FCSTD DOCUMENT  (FreeCAD 0.19R24276 (Git))
Label: Base_rear-gears_017
License: All rights reserved
LicenseURL: http://en.wikipedia.org/wiki/All_rights_reserved
objects: Part::Cylinder×88, Part::Cut×43, Part::Compound×26, Part::FeaturePython×15, Part::Box×12, Sketcher::SketchObject×7, PartDesign::Revolution×7, PartDesign::Body×7, Part::Common×6, Part::Chamfer×2, Mesh::Feature×2, Part::MultiFuse×1
note: 221 computed .brp shape members not serialized (recipe doc carries the construction recipe); baked Part::Feature solids carry a one-line shape summary decoded from their .brp

FEATURE [Part::FeaturePython] bevelgear008  # WARN: FeaturePython — macro-defined, semantics opaque (R4)
  AttacherType = Attacher::AttachEngine3D
  Placement = pos=(38,0,-244) rot=(0,-1,0;1.5708rad)
  backlash = 0.1
  beta = 12
  clearance = 0.1
  height = 30
  module = 2
  numpoints = 6
  pitch_angle = 17.29
  pressure_angle = 25
  reset_origin = true
  teeth = 13
  version = 0.0.3
FEATURE [Part::FeaturePython] Tube007  # WARN: FeaturePython — macro-defined, semantics opaque (R4)
  AttacherType = Attacher::AttachEngine3D
  Height = 40
  InnerRadius = 4.15
  OuterRadius = 8.45
  Placement = pos=(200,0,-15) rot=(0,0,1;0rad)
FEATURE [Sketcher::SketchObject] Sketch012
  FullyConstrained = false
  MapMode = 5
  Placement = pos=(0,0,0) rot=(1,0,0;1.5708rad)
  Support = -> [XZ_Plane012]
  sketch-geometry (29):
    g0: LineSegment StartX=0 StartY=-49.6356 StartZ=0 EndX=22.5 EndY=-49.6356 EndZ=0
    g1: LineSegment StartX=22.5 StartY=-49.6356 StartZ=0 EndX=22.5 EndY=-53.6356 EndZ=0
    g2: LineSegment StartX=22.5 StartY=-53.6356 StartZ=0 EndX=0 EndY=-53.6356 EndZ=0
    g3: LineSegment StartX=0 StartY=-53.6356 StartZ=0 EndX=0 EndY=-49.6356 EndZ=0
    g4: LineSegment StartX=22.5 StartY=-49.6356 StartZ=0 EndX=26.5 EndY=-49.6356 EndZ=0
    g5: LineSegment StartX=26.5 StartY=-49.6356 StartZ=0 EndX=26.5 EndY=-42.6356 EndZ=0
    g6: LineSegment StartX=26.5 StartY=-42.6356 StartZ=0 EndX=22.5 EndY=-42.6356 EndZ=0
    g7: LineSegment StartX=22.5 StartY=-42.6356 StartZ=0 EndX=22.5 EndY=-49.6356 EndZ=0
    g8: LineSegment StartX=22.5 StartY=-49.6356 StartZ=0 EndX=0 EndY=-49.6356 EndZ=0
    g9: LineSegment StartX=0 StartY=-49.6356 StartZ=0 EndX=0 EndY=-42.6356 EndZ=0
    g10: LineSegment StartX=0 StartY=-42.6356 StartZ=0 EndX=22.5 EndY=-42.6356 EndZ=0
    g11: LineSegment StartX=22.5 StartY=-42.6356 StartZ=0 EndX=22.5 EndY=-49.6356 EndZ=0
    g12: LineSegment StartX=0 StartY=-42.6356 StartZ=0 EndX=22.5 EndY=-49.6356 EndZ=0
    g13: LineSegment StartX=22.5 StartY=-49.6356 StartZ=0 EndX=21.9059 EndY=-51.5453 EndZ=0
    g14: LineSegment StartX=22.5 StartY=-49.6356 StartZ=0 EndX=23.0941 EndY=-47.7259 EndZ=0
    g15: LineSegment StartX=23.0941 StartY=-47.7259 StartZ=0 EndX=0 EndY=-42.6356 EndZ=0
    g16: LineSegment StartX=21.9059 StartY=-51.5453 StartZ=0 EndX=0 EndY=-42.6356 EndZ=0
    g17: LineSegment StartX=23.0941 StartY=-47.7259 StartZ=0 EndX=15.2817 EndY=-46.0039 EndZ=0
    g18: LineSegment StartX=15.2817 StartY=-46.0039 StartZ=0 EndX=14.1518 EndY=-49.6356 EndZ=0
    g19: LineSegment StartX=15.2817 StartY=-42.6356 StartZ=0 EndX=15.2817 EndY=-46.0039 EndZ=0
    g20: LineSegment StartX=21.9059 StartY=-51.5453 StartZ=0 EndX=21.9059 EndY=-53.6356 EndZ=0
    g21: LineSegment StartX=23.0941 StartY=-47.7259 StartZ=0 EndX=26.5 EndY=-47.7259 EndZ=0
    g22: LineSegment StartX=15.2817 StartY=-42.6356 StartZ=0 EndX=15.2817 EndY=-46.5709 EndZ=0
    g23: LineSegment StartX=15.2817 StartY=-46.5709 StartZ=0 EndX=14.4998 EndY=-48.5171 EndZ=0
    g24: LineSegment StartX=14.4998 StartY=-48.5171 StartZ=0 EndX=21.9059 EndY=-51.5453 EndZ=0
    g25: LineSegment StartX=26.275 StartY=-49.2912 StartZ=0 EndX=26.5 EndY=-42.6356 EndZ=0
    g26: LineSegment StartX=26.5 StartY=-42.6356 StartZ=0 EndX=15.2817 EndY=-42.6356 EndZ=0
    g27: LineSegment StartX=26.275 StartY=-49.2912 StartZ=0 EndX=26.275 EndY=-53.3318 EndZ=0
    g28: LineSegment StartX=21.9059 StartY=-51.5453 StartZ=0 EndX=26.275 EndY=-53.3318 EndZ=0
  constraints (77):
    c: Coincident(g0,g1)
    c: Coincident(g1,g2)
    c: Coincident(g2,g3)
    c: Coincident(g3,g0)
    c: Horizontal(g0)
    c: Horizontal(g2)
    c: Vertical(g1)
    c: Vertical(g3)
    c: PointOnObject(g0,g-2)
    c: Distance(g0) = 22.5
    c: Distance(g1) = 4
    c: Coincident(g4,g5)
    c: Coincident(g5,g6)
    c: Coincident(g6,g7)
    c: Coincident(g7,g4)
    c: Horizontal(g4)
    c: Horizontal(g6)
    c: Vertical(g5)
    c: Vertical(g7)
    c: Coincident(g4,g0)
    c: Distance(g7) = 7
    c: Distance(g6) = 4
    c: Coincident(g8,g9)
    c: Coincident(g9,g10)
    c: Coincident(g10,g11)
    c: Coincident(g11,g8)
    c: Horizontal(g8)
    c: Horizontal(g10)
    c: Vertical(g9)
    c: Vertical(g11)
    c: Coincident(g8,g0)
    c: PointOnObject(g9,g-2)
    c: Distance(g9) = 7
    c: Coincident(g12,g9)
    c: Coincident(g12,g0)
    c: Coincident(g13,g0)
    c: Perpendicular(g13,g12)
    c: Distance(g13) = 2
    c: Coincident(g14,g0)
    c: Distance(g14) = 2
    c: Perpendicular(g14,g12)
    c: Coincident(g15,g14)
    c: Coincident(g15,g9)
    c: Coincident(g16,g13)
    c: Coincident(g16,g9)
    c: Coincident(g17,g14)
    c: PointOnObject(g17,g15)
    c: Distance(g17) = 8
    c: Coincident(g18,g17)
    c: PointOnObject(g18,g0)
    c: Perpendicular(g18,g12)
    c: PointOnObject(g19,g10)
    c: Coincident(g19,g17)
    c: Vertical(g19)
    c: Coincident(g20,g13)
    c: PointOnObject(g20,g2)
    c: Vertical(g20)
    c: Coincident(g21,g14)
    c: PointOnObject(g21,g5)
    c: Horizontal(g21)
    c: Coincident(g19,g22)
    c: Coincident(g23,g22)
    c: PointOnObject(g23,g18)
    c: Coincident(g24,g23)
    c: Coincident(g24,g13)
    c: Coincident(g25,g5)
    c: Coincident(g26,g25)
    c: Coincident(g26,g22)
    c: Vertical(g22)
    c: Angle(g15,g10) = 0.216946
    c: Angle(g12,g10) = 0.301619
    c: Angle(g9,g12) = 1.26918
    c: Coincident(g27,g25)
    c: Vertical(g27)
    c: Coincident(g28,g24)
    c: Coincident(g28,g27)
    c: Parallel(g24,g28)
FEATURE [PartDesign::Revolution] Revolution012
  Angle = 360
  Axis = (22.5,0,0)
  Base = (0,9.5e-15,-42.6356)
  Placement = pos=(0,0,0) rot=(1,0,0;1.5708rad)
  Profile = -> Sketch012
  ReferenceAxis = -> Sketch012 [Axis10]
  Reversed = true
FEATURE [PartDesign::Body] Body010
  Group = -> [Revolution012,Sketch012]
  Origin = -> Origin010
  Placement = pos=(-9.5,0,-201.4) rot=(0,0,1;0rad)
  Tip = -> Revolution012
FEATURE [Part::Box] Box255  label="Krychle255"
  AttacherType = Attacher::AttachEngine3D
  Height = 6
  Length = 6
  Placement = pos=(196.5,-3,18) rot=(0,0,1;1.5708rad)
  Width = 2
FEATURE [Part::Cylinder] Cylinder656  label="Válec656"
  Angle = 360
  AttacherType = Attacher::AttachEngine3D
  Height = 10
  Placement = pos=(0,118,50) rot=(1,0,0;1.5708rad)
  Radius = 4.1
FEATURE [Part::Cylinder] Cylinder657  label="Válec657"
  Angle = 360
  AttacherType = Attacher::AttachEngine3D
  Height = 4
  Placement = pos=(0,110,50) rot=(1,0,0;1.5708rad)
  Radius = 10.5
FEATURE [Part::Cut] Cut265
  Base = -> Cylinder657
  Tool = -> Cylinder656
FEATURE [Part::Box] Box256  label="Krychle256"
  AttacherType = Attacher::AttachEngine3D
  Height = 40
  Length = 40
  Placement = pos=(-20,110,30) rot=(0,0,1;0rad)
  Width = 20
FEATURE [Part::Cut] Cut266
  Base = -> Cut265
  Tool = -> Box256
FEATURE [Part::Chamfer] Chamfer
  Base = -> Cut266
  Edges = 1 edges r=2.5: [Edge3]
FEATURE [Sketcher::SketchObject] Sketch011
  FullyConstrained = false
  MapMode = 5
  Placement = pos=(0,0,0) rot=(1,0,0;1.5708rad)
  Support = -> [XZ_Plane013]
  sketch-geometry (29):
    g0: LineSegment StartX=0 StartY=-49.6356 StartZ=0 EndX=22.5 EndY=-49.6356 EndZ=0
    g1: LineSegment StartX=22.5 StartY=-49.6356 StartZ=0 EndX=22.5 EndY=-53.6356 EndZ=0
    g2: LineSegment StartX=22.5 StartY=-53.6356 StartZ=0 EndX=0 EndY=-53.6356 EndZ=0
    g3: LineSegment StartX=0 StartY=-53.6356 StartZ=0 EndX=0 EndY=-49.6356 EndZ=0
    g4: LineSegment StartX=22.5 StartY=-49.6356 StartZ=0 EndX=26.5 EndY=-49.6356 EndZ=0
    g5: LineSegment StartX=26.5 StartY=-49.6356 StartZ=0 EndX=26.5 EndY=-42.6356 EndZ=0
    g6: LineSegment StartX=26.5 StartY=-42.6356 StartZ=0 EndX=22.5 EndY=-42.6356 EndZ=0
    g7: LineSegment StartX=22.5 StartY=-42.6356 StartZ=0 EndX=22.5 EndY=-49.6356 EndZ=0
    g8: LineSegment StartX=22.5 StartY=-49.6356 StartZ=0 EndX=0 EndY=-49.6356 EndZ=0
    g9: LineSegment StartX=0 StartY=-49.6356 StartZ=0 EndX=0 EndY=-42.6356 EndZ=0
    g10: LineSegment StartX=0 StartY=-42.6356 StartZ=0 EndX=22.5 EndY=-42.6356 EndZ=0
    g11: LineSegment StartX=22.5 StartY=-42.6356 StartZ=0 EndX=22.5 EndY=-49.6356 EndZ=0
    g12: LineSegment StartX=0 StartY=-42.6356 StartZ=0 EndX=22.5 EndY=-49.6356 EndZ=0
    g13: LineSegment StartX=22.5 StartY=-49.6356 StartZ=0 EndX=21.9059 EndY=-51.5453 EndZ=0
    g14: LineSegment StartX=22.5 StartY=-49.6356 StartZ=0 EndX=23.0941 EndY=-47.7259 EndZ=0
    g15: LineSegment StartX=23.0941 StartY=-47.7259 StartZ=0 EndX=0 EndY=-42.6356 EndZ=0
    g16: LineSegment StartX=21.9059 StartY=-51.5453 StartZ=0 EndX=0 EndY=-42.6356 EndZ=0
    g17: LineSegment StartX=23.0941 StartY=-47.7259 StartZ=0 EndX=15.2817 EndY=-46.0039 EndZ=0
    g18: LineSegment StartX=15.2817 StartY=-46.0039 StartZ=0 EndX=14.1518 EndY=-49.6356 EndZ=0
    g19: LineSegment StartX=15.2817 StartY=-42.6356 StartZ=0 EndX=15.2817 EndY=-46.0039 EndZ=0
    g20: LineSegment StartX=21.9059 StartY=-51.5453 StartZ=0 EndX=21.9059 EndY=-53.6356 EndZ=0
    g21: LineSegment StartX=23.0941 StartY=-47.7259 StartZ=0 EndX=26.5 EndY=-47.7259 EndZ=0
    g22: LineSegment StartX=15.2817 StartY=-42.6356 StartZ=0 EndX=15.2817 EndY=-46.5709 EndZ=0
    g23: LineSegment StartX=15.2817 StartY=-46.5709 StartZ=0 EndX=14.4998 EndY=-48.5171 EndZ=0
    g24: LineSegment StartX=14.4998 StartY=-48.5171 StartZ=0 EndX=21.9059 EndY=-51.5453 EndZ=0
    g25: LineSegment StartX=26.275 StartY=-49.2912 StartZ=0 EndX=26.5 EndY=-42.6356 EndZ=0
    g26: LineSegment StartX=26.5 StartY=-42.6356 StartZ=0 EndX=15.2817 EndY=-42.6356 EndZ=0
    g27: LineSegment StartX=26.275 StartY=-49.2912 StartZ=0 EndX=26.275 EndY=-53.3318 EndZ=0
    g28: LineSegment StartX=21.9059 StartY=-51.5453 StartZ=0 EndX=26.275 EndY=-53.3318 EndZ=0
  constraints (77):
    c: Coincident(g0,g1)
    c: Coincident(g1,g2)
    c: Coincident(g2,g3)
    c: Coincident(g3,g0)
    c: Horizontal(g0)
    c: Horizontal(g2)
    c: Vertical(g1)
    c: Vertical(g3)
    c: PointOnObject(g0,g-2)
    c: Distance(g0) = 22.5
    c: Distance(g1) = 4
    c: Coincident(g4,g5)
    c: Coincident(g5,g6)
    c: Coincident(g6,g7)
    c: Coincident(g7,g4)
    c: Horizontal(g4)
    c: Horizontal(g6)
    c: Vertical(g5)
    c: Vertical(g7)
    c: Coincident(g4,g0)
    c: Distance(g7) = 7
    c: Distance(g6) = 4
    c: Coincident(g8,g9)
    c: Coincident(g9,g10)
    c: Coincident(g10,g11)
    c: Coincident(g11,g8)
    c: Horizontal(g8)
    c: Horizontal(g10)
    c: Vertical(g9)
    c: Vertical(g11)
    c: Coincident(g8,g0)
    c: PointOnObject(g9,g-2)
    c: Distance(g9) = 7
    c: Coincident(g12,g9)
    c: Coincident(g12,g0)
    c: Coincident(g13,g0)
    c: Perpendicular(g13,g12)
    c: Distance(g13) = 2
    c: Coincident(g14,g0)
    c: Distance(g14) = 2
    c: Perpendicular(g14,g12)
    c: Coincident(g15,g14)
    c: Coincident(g15,g9)
    c: Coincident(g16,g13)
    c: Coincident(g16,g9)
    c: Coincident(g17,g14)
    c: PointOnObject(g17,g15)
    c: Distance(g17) = 8
    c: Coincident(g18,g17)
    c: PointOnObject(g18,g0)
    c: Perpendicular(g18,g12)
    c: PointOnObject(g19,g10)
    c: Coincident(g19,g17)
    c: Vertical(g19)
    c: Coincident(g20,g13)
    c: PointOnObject(g20,g2)
    c: Vertical(g20)
    c: Coincident(g21,g14)
    c: PointOnObject(g21,g5)
    c: Horizontal(g21)
    c: Coincident(g19,g22)
    c: Coincident(g23,g22)
    c: PointOnObject(g23,g18)
    c: Coincident(g24,g23)
    c: Coincident(g24,g13)
    c: Coincident(g25,g5)
    c: Coincident(g26,g25)
    c: Coincident(g26,g22)
    c: Vertical(g22)
    c: Angle(g15,g10) = 0.216946
    c: Angle(g12,g10) = 0.301619
    c: Angle(g9,g12) = 1.26918
    c: Coincident(g27,g25)
    c: Vertical(g27)
    c: Coincident(g28,g24)
    c: Coincident(g28,g27)
    c: Parallel(g24,g28)
FEATURE [PartDesign::Revolution] Revolution011
  Angle = 360
  Axis = (22.5,0,0)
  Base = (0,9.5e-15,-42.6356)
  Placement = pos=(0,0,0) rot=(1,0,0;1.5708rad)
  Profile = -> Sketch011
  ReferenceAxis = -> Sketch011 [Axis10]
  Reversed = true
FEATURE [PartDesign::Body] Body009
  Group = -> [Revolution011,Sketch011]
  Origin = -> Origin009
  Placement = pos=(-1.4,0,-201.4) rot=(0,0,1;0rad)
  Tip = -> Revolution011
FEATURE [Part::Box] Box254  label="Krychle254"
  AttacherType = Attacher::AttachEngine3D
  Height = 6
  Length = 6
  Placement = pos=(196.5,-3,12) rot=(0,0,1;1.5708rad)
  Width = 2
FEATURE [Part::Compound] Compound030
  Links = -> [Box255,Box254]
  Placement = pos=(0,0,-27) rot=(0,0,1;0rad)
FEATURE [Part::Cylinder] Cylinder655  label="Válec655"
  Angle = 360
  AttacherType = Attacher::AttachEngine3D
  Height = 100
  Placement = pos=(100,0,15) rot=(0.57735,0.57735,0.57735;2.0944rad)
  Radius = 1.5
FEATURE [Part::Box] Box253  label="Krychle253"
  AttacherType = Attacher::AttachEngine3D
  Height = 32
  Length = 2
  Placement = pos=(194.5,-4,-4) rot=(0,0,1;0rad)
  Width = 8
FEATURE [Part::MultiFuse] Fusion003
  Shapes = -> [Tube007,Box253]
FEATURE [Part::Cut] Cut263
  Base = -> Fusion003
  Tool = -> Compound030
FEATURE [Part::Cylinder] Cylinder654  label="Válec654"
  Angle = 360
  AttacherType = Attacher::AttachEngine3D
  Height = 100
  Placement = pos=(100,0,21) rot=(0.57735,0.57735,0.57735;2.0944rad)
  Radius = 1.5
FEATURE [Part::Compound] Compound031
  Links = -> [Cylinder654,Cylinder655]
  Placement = pos=(0,0,-27) rot=(0,0,1;0rad)
FEATURE [Part::Cut] Cut264  label="super_spojka003"
  Base = -> Cut263
  Placement = pos=(-200,133,50) rot=(1,0,0;1.5708rad)
  Tool = -> Compound031
FEATURE [Part::Common] Common
  Base = -> bevelgear008
  Tool = -> Body009
FEATURE [Part::Cut] Cut262
  Base = -> Common
  Placement = pos=(0,81.1,294) rot=(0,0,1;1.5708rad)
  Tool = -> Body010
FEATURE [Part::Compound] Compound032  label="Base_rear-gear-small1"
  Links = -> [Cut262,Cut264,Chamfer]
FEATURE [Sketcher::SketchObject] Sketch013
  FullyConstrained = false
  MapMode = 5
  Placement = pos=(0,0,0) rot=(1,0,0;1.5708rad)
  Support = -> [XZ_Plane014]
  sketch-geometry (29):
    g0: LineSegment StartX=0 StartY=-63.1814 StartZ=0 EndX=22.5 EndY=-63.1814 EndZ=0
    g1: LineSegment StartX=22.5 StartY=-63.1814 StartZ=0 EndX=22.5 EndY=-67.1814 EndZ=0
    g2: LineSegment StartX=22.5 StartY=-67.1814 StartZ=0 EndX=0 EndY=-67.1814 EndZ=0
    g3: LineSegment StartX=0 StartY=-67.1814 StartZ=0 EndX=0 EndY=-63.1814 EndZ=0
    g4: LineSegment StartX=22.5 StartY=-63.1814 StartZ=0 EndX=26.5 EndY=-63.1814 EndZ=0
    g5: LineSegment StartX=26.5 StartY=-63.1814 StartZ=0 EndX=26.5 EndY=-58.1814 EndZ=0
    g6: LineSegment StartX=26.5 StartY=-58.1814 StartZ=0 EndX=22.5 EndY=-58.1814 EndZ=0
    g7: LineSegment StartX=22.5 StartY=-58.1814 StartZ=0 EndX=22.5 EndY=-63.1814 EndZ=0
    g8: LineSegment StartX=22.5 StartY=-63.1814 StartZ=0 EndX=0 EndY=-63.1814 EndZ=0
    g9: LineSegment StartX=0 StartY=-63.1814 StartZ=0 EndX=0 EndY=-56.1814 EndZ=0
    g10: LineSegment StartX=0 StartY=-56.1814 StartZ=0 EndX=22.5 EndY=-56.1814 EndZ=0
    g11: LineSegment StartX=22.5 StartY=-56.1814 StartZ=0 EndX=22.5 EndY=-63.1814 EndZ=0
    g12: LineSegment StartX=0 StartY=-56.1814 StartZ=0 EndX=22.5 EndY=-63.1814 EndZ=0
    g13: LineSegment StartX=22.5 StartY=-63.1814 StartZ=0 EndX=21.9059 EndY=-65.0911 EndZ=0
    g14: LineSegment StartX=22.5 StartY=-63.1814 StartZ=0 EndX=23.0941 EndY=-61.2717 EndZ=0
    g15: LineSegment StartX=23.0941 StartY=-61.2717 StartZ=0 EndX=0 EndY=-56.1814 EndZ=0
    g16: LineSegment StartX=21.9059 StartY=-65.0911 StartZ=0 EndX=0 EndY=-56.1814 EndZ=0
    g17: LineSegment StartX=23.0941 StartY=-61.2717 StartZ=0 EndX=15.2817 EndY=-59.5497 EndZ=0
    g18: LineSegment StartX=15.2817 StartY=-59.5497 StartZ=0 EndX=14.1518 EndY=-63.1814 EndZ=0
    g19: LineSegment StartX=15.2817 StartY=-56.1814 StartZ=0 EndX=15.2817 EndY=-59.5497 EndZ=0
    g20: LineSegment StartX=21.9059 StartY=-65.0911 StartZ=0 EndX=21.9059 EndY=-67.1814 EndZ=0
    g21: LineSegment StartX=23.0941 StartY=-61.2717 StartZ=0 EndX=26.5 EndY=-61.2717 EndZ=0
    g22: LineSegment StartX=21.9059 StartY=-67.1814 StartZ=0 EndX=21.9059 EndY=-65.0911 EndZ=0
    g23: LineSegment StartX=21.9059 StartY=-65.0911 StartZ=0 EndX=23.0941 EndY=-61.2717 EndZ=0
    g24: LineSegment StartX=23.0941 StartY=-61.2717 StartZ=0 EndX=15.2817 EndY=-59.5497 EndZ=0
    g25: LineSegment StartX=15.2817 StartY=-59.5497 StartZ=0 EndX=14.1518 EndY=-63.1814 EndZ=0
    g26: LineSegment StartX=14.1518 StartY=-63.1814 StartZ=0 EndX=0 EndY=-63.1814 EndZ=0
    g27: LineSegment StartX=0 StartY=-63.1814 StartZ=0 EndX=0 EndY=-67.1814 EndZ=0
    g28: LineSegment StartX=0 StartY=-67.1814 StartZ=0 EndX=21.9059 EndY=-67.1814 EndZ=0
  constraints (77):
    c: Coincident(g0,g1)
    c: Coincident(g1,g2)
    c: Coincident(g2,g3)
    c: Coincident(g3,g0)
    c: Horizontal(g0)
    c: Horizontal(g2)
    c: Vertical(g1)
    c: Vertical(g3)
    c: PointOnObject(g0,g-2)
    c: Distance(g0) = 22.5
    c: Distance(g1) = 4
    c: Coincident(g4,g5)
    c: Coincident(g5,g6)
    c: Coincident(g6,g7)
    c: Coincident(g7,g4)
    c: Horizontal(g4)
    c: Horizontal(g6)
    c: Vertical(g5)
    c: Vertical(g7)
    c: Coincident(g4,g0)
    c: Distance(g7) = 5
    c: Distance(g6) = 4
    c: Coincident(g8,g9)
    c: Coincident(g9,g10)
    c: Coincident(g10,g11)
    c: Coincident(g11,g8)
    c: Horizontal(g8)
    c: Horizontal(g10)
    c: Vertical(g9)
    c: Vertical(g11)
    c: Coincident(g8,g0)
    c: PointOnObject(g9,g-2)
    c: Distance(g9) = 7
    c: Coincident(g12,g9)
    c: Coincident(g12,g0)
    c: Coincident(g13,g0)
    c: Perpendicular(g13,g12)
    c: Distance(g13) = 2
    c: Coincident(g14,g0)
    c: Distance(g14) = 2
    c: Perpendicular(g14,g12)
    c: Coincident(g15,g14)
    c: Coincident(g15,g9)
    c: Coincident(g16,g13)
    c: Coincident(g16,g9)
    c: Coincident(g17,g14)
    c: PointOnObject(g17,g15)
    c: Distance(g17) = 8
    c: Coincident(g18,g17)
    c: PointOnObject(g18,g0)
    c: Perpendicular(g18,g12)
    c: PointOnObject(g19,g10)
    c: Coincident(g19,g17)
    c: Vertical(g19)
    c: Coincident(g20,g13)
    c: PointOnObject(g20,g2)
    c: Vertical(g20)
    c: Coincident(g21,g14)
    c: PointOnObject(g21,g5)
    c: Horizontal(g21)
    c: Angle(g15,g10) = 0.216946
    c: Angle(g12,g10) = 0.301619
    c: Angle(g9,g12) = 1.26918
    c: Coincident(g22,g20)
    c: Coincident(g22,g13)
    c: Coincident(g22,g23)
    c: Coincident(g23,g14)
    c: Coincident(g23,g24)
    c: Coincident(g24,g17)
    c: Coincident(g24,g25)
    c: Coincident(g25,g18)
    c: Coincident(g26,g25)
    c: Coincident(g26,g0)
    c: Coincident(g27,g26)
    c: Coincident(g27,g2)
    c: Coincident(g28,g27)
    c: Coincident(g28,g22)
FEATURE [PartDesign::Revolution] Revolution013
  Angle = 360
  Axis = (0,-9e-16,4)
  Base = (0,1.49e-14,-67.1814)
  Placement = pos=(0,0,0) rot=(1,0,0;1.5708rad)
  Profile = -> Sketch013
  ReferenceAxis = -> Sketch013 [Axis3]
  Reversed = true
FEATURE [Part::Cylinder] Cylinder584  label="Válec584"
  Angle = 360
  AttacherType = Attacher::AttachEngine3D
  Height = 30
  Placement = pos=(0,72,232) rot=(0,0,1;0rad)
  Radius = 1.5
FEATURE [Part::Cylinder] Cylinder588  label="Válec588"
  Angle = 360
  AttacherType = Attacher::AttachEngine3D
  Height = 30
  Placement = pos=(-11,83,232) rot=(0,0,1;0rad)
  Radius = 1.5
FEATURE [Part::Cylinder] Cylinder590  label="Válec590"
  Angle = 360
  AttacherType = Attacher::AttachEngine3D
  Height = 30
  Placement = pos=(11,83,232) rot=(0,0,1;0rad)
  Radius = 1.5
FEATURE [Part::Cylinder] Cylinder573  label="Válec573"
  Angle = 360
  AttacherType = Attacher::AttachEngine3D
  Height = 3
  Placement = pos=(0,72,232) rot=(0,0,1;0rad)
  Radius = 3
FEATURE [Part::Cylinder] Cylinder587  label="Válec587"
  Angle = 360
  AttacherType = Attacher::AttachEngine3D
  Height = 30
  Placement = pos=(0,72,232) rot=(0,0,1;0rad)
  Radius = 1.5
FEATURE [Part::Cylinder] Cylinder589  label="Válec589"
  Angle = 360
  AttacherType = Attacher::AttachEngine3D
  Height = 30
  Placement = pos=(0,94,232) rot=(0,0,1;0rad)
  Radius = 1.5
FEATURE [Part::Compound] Compound360
  Links = -> [Cylinder588,Cylinder590,Cylinder587,Cylinder589]
FEATURE [Part::FeaturePython] bevelgear010  # WARN: FeaturePython — macro-defined, semantics opaque (R4)
  AttacherType = Attacher::AttachEngine3D
  Placement = pos=(0,0,-254.4) rot=(1,0,0;3.14159rad)
  backlash = 0
  beta = 12
  clearance = 0.1
  height = 16
  module = 0.1
  numpoints = 6
  pitch_angle = 72.71
  pressure_angle = 21
  reset_origin = true
  teeth = 36
  version = 0.0.3
FEATURE [PartDesign::Body] Body011
  Group = -> [Revolution013,Sketch013]
  Origin = -> Origin011
  Placement = pos=(0,0,-199.6) rot=(0,0,1;0rad)
  Tip = -> Revolution013
FEATURE [Part::Common] Common001
  Base = -> Body011
  Placement = pos=(0,83,507) rot=(0,0,1;0rad)
  Tool = -> bevelgear010
FEATURE [Part::Cylinder] Cylinder576  label="Válec576"
  Angle = 360
  AttacherType = Attacher::AttachEngine3D
  Height = 3
  Placement = pos=(11,83,232) rot=(0,0,1;0rad)
  Radius = 3
FEATURE [Part::Cylinder] Cylinder569  label="Válec569"
  Angle = 360
  AttacherType = Attacher::AttachEngine3D
  Height = 10
  Placement = pos=(0,83,242) rot=(0,0,1;0rad)
  Radius = 15.1
FEATURE [Part::Cylinder] Cylinder578  label="Válec578"
  Angle = 360
  AttacherType = Attacher::AttachEngine3D
  Height = 3
  Placement = pos=(-11,83,232) rot=(0,0,1;0rad)
  Radius = 3
FEATURE [Part::Cylinder] Cylinder585  label="Válec585"
  Angle = 360
  AttacherType = Attacher::AttachEngine3D
  Height = 30
  Placement = pos=(-11,83,232) rot=(0,0,1;0rad)
  Radius = 1.5
FEATURE [Part::Cylinder] Cylinder582  label="Válec582"
  Angle = 360
  AttacherType = Attacher::AttachEngine3D
  Height = 3
  Placement = pos=(0,94,232) rot=(0,0,1;0rad)
  Radius = 3
FEATURE [Part::Compound] Compound359
  Links = -> [Cylinder578,Cylinder576,Cylinder573,Cylinder582]
  Placement = pos=(0,0,17) rot=(0,0,1;0rad)
FEATURE [Part::Cylinder] Cylinder577  label="Válec577"
  Angle = 360
  AttacherType = Attacher::AttachEngine3D
  Height = 17
  Placement = pos=(0,83,252) rot=(0,0,1;0rad)
  Radius = 8
FEATURE [Part::Cylinder] Cylinder581  label="Válec581"
  Angle = 360
  AttacherType = Attacher::AttachEngine3D
  Height = 40
  Placement = pos=(0,83,232) rot=(0,0,1;0rad)
  Radius = 2.65
FEATURE [Part::Cut] Cut220
  Base = -> Cylinder577
  Tool = -> Cylinder581
FEATURE [Part::Cylinder] Cylinder583  label="Válec583"
  Angle = 360
  AttacherType = Attacher::AttachEngine3D
  Height = 30
  Placement = pos=(0,94,232) rot=(0,0,1;0rad)
  Radius = 1.5
FEATURE [Part::Cylinder] Cylinder586  label="Válec586"
  Angle = 360
  AttacherType = Attacher::AttachEngine3D
  Height = 30
  Placement = pos=(0,83,232) rot=(0,0,1;0rad)
  Radius = 2.65
FEATURE [Part::Cylinder] Cylinder580  label="Válec580"
  Angle = 360
  AttacherType = Attacher::AttachEngine3D
  Height = 30
  Placement = pos=(11,83,232) rot=(0,0,1;0rad)
  Radius = 1.5
FEATURE [Part::Compound] Compound358
  Links = -> [Cylinder585,Cylinder580,Cylinder584,Cylinder583]
FEATURE [Part::Cut] Cut221
  Base = -> Cylinder569
  Tool = -> Compound358
FEATURE [Part::Cut] Cut223
  Base = -> Cut221
  Tool = -> Compound359
FEATURE [Part::Cut] Cut226
  Base = -> Cut223
  Tool = -> Cylinder586
FEATURE [Part::Cut] Cut227
  Base = -> Common001
  Tool = -> Compound360
FEATURE [Part::Compound] Compound  label="Base_rear-gear-large-old"
  Links = -> [Cut227,Cut226,Cut220]
  Placement = pos=(0,0,-205) rot=(0,0,1;0rad)
FEATURE [Part::Cylinder] Cylinder600  label="Válec600"
  Angle = 360
  AttacherType = Attacher::AttachEngine3D
  Height = 30
  Placement = pos=(0,72,15) rot=(0,0,1;0rad)
  Radius = 1.5
FEATURE [Part::Box] Box  label="Krychle"
  AttacherType = Attacher::AttachEngine3D
  Height = 20
  Length = 6
  Placement = pos=(8,80,38) rot=(0,0,1;0rad)
  Width = 6
FEATURE [Part::Box] Box002  label="Krychle002"
  AttacherType = Attacher::AttachEngine3D
  Height = 20
  Length = 6
  Placement = pos=(-3,69,38) rot=(0,0,1;0rad)
  Width = 6
FEATURE [Part::Cylinder] Cylinder598  label="Válec598"
  Angle = 360
  AttacherType = Attacher::AttachEngine3D
  Height = 30
  Placement = pos=(0,72,15) rot=(0,0,1;0rad)
  Radius = 1.5
FEATURE [Part::Box] Box003  label="Krychle003"
  AttacherType = Attacher::AttachEngine3D
  Height = 20
  Length = 6
  Placement = pos=(-3,91,38) rot=(0,0,1;0rad)
  Width = 6
FEATURE [Part::Cylinder] Cylinder599  label="Válec599"
  Angle = 360
  AttacherType = Attacher::AttachEngine3D
  Height = 30
  Placement = pos=(0,94,15) rot=(0,0,1;0rad)
  Radius = 1.5
FEATURE [Sketcher::SketchObject] Sketch014
  FullyConstrained = false
  MapMode = 5
  Placement = pos=(0,0,0) rot=(1,0,0;1.5708rad)
  Support = -> [XZ_Plane015]
  sketch-geometry (29):
    g0: LineSegment StartX=0 StartY=-63.1814 StartZ=0 EndX=22.5 EndY=-63.1814 EndZ=0
    g1: LineSegment StartX=22.5 StartY=-63.1814 StartZ=0 EndX=22.5 EndY=-67.1814 EndZ=0
    g2: LineSegment StartX=22.5 StartY=-67.1814 StartZ=0 EndX=0 EndY=-67.1814 EndZ=0
    g3: LineSegment StartX=0 StartY=-67.1814 StartZ=0 EndX=0 EndY=-63.1814 EndZ=0
    g4: LineSegment StartX=22.5 StartY=-63.1814 StartZ=0 EndX=26.5 EndY=-63.1814 EndZ=0
    g5: LineSegment StartX=26.5 StartY=-63.1814 StartZ=0 EndX=26.5 EndY=-58.1814 EndZ=0
    g6: LineSegment StartX=26.5 StartY=-58.1814 StartZ=0 EndX=22.5 EndY=-58.1814 EndZ=0
    g7: LineSegment StartX=22.5 StartY=-58.1814 StartZ=0 EndX=22.5 EndY=-63.1814 EndZ=0
    g8: LineSegment StartX=22.5 StartY=-63.1814 StartZ=0 EndX=0 EndY=-63.1814 EndZ=0
    g9: LineSegment StartX=0 StartY=-63.1814 StartZ=0 EndX=0 EndY=-56.1814 EndZ=0
    g10: LineSegment StartX=0 StartY=-56.1814 StartZ=0 EndX=22.5 EndY=-56.1814 EndZ=0
    g11: LineSegment StartX=22.5 StartY=-56.1814 StartZ=0 EndX=22.5 EndY=-63.1814 EndZ=0
    g12: LineSegment StartX=0 StartY=-56.1814 StartZ=0 EndX=22.5 EndY=-63.1814 EndZ=0
    g13: LineSegment StartX=22.5 StartY=-63.1814 StartZ=0 EndX=21.9059 EndY=-65.0911 EndZ=0
    g14: LineSegment StartX=22.5 StartY=-63.1814 StartZ=0 EndX=23.0941 EndY=-61.2717 EndZ=0
    g15: LineSegment StartX=23.0941 StartY=-61.2717 StartZ=0 EndX=0 EndY=-56.1814 EndZ=0
    g16: LineSegment StartX=21.9059 StartY=-65.0911 StartZ=0 EndX=0 EndY=-56.1814 EndZ=0
    g17: LineSegment StartX=23.0941 StartY=-61.2717 StartZ=0 EndX=15.2817 EndY=-59.5497 EndZ=0
    g18: LineSegment StartX=15.2817 StartY=-59.5497 StartZ=0 EndX=14.1518 EndY=-63.1814 EndZ=0
    g19: LineSegment StartX=15.2817 StartY=-56.1814 StartZ=0 EndX=15.2817 EndY=-59.5497 EndZ=0
    g20: LineSegment StartX=21.9059 StartY=-65.0911 StartZ=0 EndX=21.9059 EndY=-67.1814 EndZ=0
    g21: LineSegment StartX=23.0941 StartY=-61.2717 StartZ=0 EndX=26.5 EndY=-61.2717 EndZ=0
    g22: LineSegment StartX=21.9059 StartY=-67.1814 StartZ=0 EndX=21.9059 EndY=-65.0911 EndZ=0
    g23: LineSegment StartX=21.9059 StartY=-65.0911 StartZ=0 EndX=23.0941 EndY=-61.2717 EndZ=0
    g24: LineSegment StartX=23.0941 StartY=-61.2717 StartZ=0 EndX=15.2817 EndY=-59.5497 EndZ=0
    g25: LineSegment StartX=15.2817 StartY=-59.5497 StartZ=0 EndX=14.1518 EndY=-63.1814 EndZ=0
    g26: LineSegment StartX=14.1518 StartY=-63.1814 StartZ=0 EndX=0 EndY=-63.1814 EndZ=0
    g27: LineSegment StartX=0 StartY=-63.1814 StartZ=0 EndX=0 EndY=-67.1814 EndZ=0
    g28: LineSegment StartX=0 StartY=-67.1814 StartZ=0 EndX=21.9059 EndY=-67.1814 EndZ=0
  constraints (77):
    c: Coincident(g0,g1)
    c: Coincident(g1,g2)
    c: Coincident(g2,g3)
    c: Coincident(g3,g0)
    c: Horizontal(g0)
    c: Horizontal(g2)
    c: Vertical(g1)
    c: Vertical(g3)
    c: PointOnObject(g0,g-2)
    c: Distance(g0) = 22.5
    c: Distance(g1) = 4
    c: Coincident(g4,g5)
    c: Coincident(g5,g6)
    c: Coincident(g6,g7)
    c: Coincident(g7,g4)
    c: Horizontal(g4)
    c: Horizontal(g6)
    c: Vertical(g5)
    c: Vertical(g7)
    c: Coincident(g4,g0)
    c: Distance(g7) = 5
    c: Distance(g6) = 4
    c: Coincident(g8,g9)
    c: Coincident(g9,g10)
    c: Coincident(g10,g11)
    c: Coincident(g11,g8)
    c: Horizontal(g8)
    c: Horizontal(g10)
    c: Vertical(g9)
    c: Vertical(g11)
    c: Coincident(g8,g0)
    c: PointOnObject(g9,g-2)
    c: Distance(g9) = 7
    c: Coincident(g12,g9)
    c: Coincident(g12,g0)
    c: Coincident(g13,g0)
    c: Perpendicular(g13,g12)
    c: Distance(g13) = 2
    c: Coincident(g14,g0)
    c: Distance(g14) = 2
    c: Perpendicular(g14,g12)
    c: Coincident(g15,g14)
    c: Coincident(g15,g9)
    c: Coincident(g16,g13)
    c: Coincident(g16,g9)
    c: Coincident(g17,g14)
    c: PointOnObject(g17,g15)
    c: Distance(g17) = 8
    c: Coincident(g18,g17)
    c: PointOnObject(g18,g0)
    c: Perpendicular(g18,g12)
    c: PointOnObject(g19,g10)
    c: Coincident(g19,g17)
    c: Vertical(g19)
    c: Coincident(g20,g13)
    c: PointOnObject(g20,g2)
    c: Vertical(g20)
    c: Coincident(g21,g14)
    c: PointOnObject(g21,g5)
    c: Horizontal(g21)
    c: Angle(g15,g10) = 0.216946
    c: Angle(g12,g10) = 0.301619
    c: Angle(g9,g12) = 1.26918
    c: Coincident(g22,g20)
    c: Coincident(g22,g13)
    c: Coincident(g22,g23)
    c: Coincident(g23,g14)
    c: Coincident(g23,g24)
    c: Coincident(g24,g17)
    c: Coincident(g24,g25)
    c: Coincident(g25,g18)
    c: Coincident(g26,g25)
    c: Coincident(g26,g0)
    c: Coincident(g27,g26)
    c: Coincident(g27,g2)
    c: Coincident(g28,g27)
    c: Coincident(g28,g22)
FEATURE [PartDesign::Revolution] Revolution014
  Angle = 360
  Axis = (0,-9e-16,4)
  Base = (0,1.49e-14,-67.1814)
  Placement = pos=(0,0,0) rot=(1,0,0;1.5708rad)
  Profile = -> Sketch014
  ReferenceAxis = -> Sketch014 [Axis3]
  Reversed = true
FEATURE [Part::Cylinder] Cylinder591  label="Válec591"
  Angle = 360
  AttacherType = Attacher::AttachEngine3D
  Height = 30
  Placement = pos=(-11,83,15) rot=(0,0,1;0rad)
  Radius = 1.5
FEATURE [Part::Cylinder] Cylinder595  label="Válec595"
  Angle = 360
  AttacherType = Attacher::AttachEngine3D
  Height = 30
  Placement = pos=(0,94,15) rot=(0,0,1;0rad)
  Radius = 1.5
FEATURE [Part::Cylinder] Cylinder593  label="Válec593"
  Angle = 360
  AttacherType = Attacher::AttachEngine3D
  Height = 30
  Placement = pos=(11,83,15) rot=(0,0,1;0rad)
  Radius = 1.5
FEATURE [Part::Cylinder] Cylinder592  label="Válec592"
  Angle = 360
  AttacherType = Attacher::AttachEngine3D
  Height = 30
  Placement = pos=(-11,83,15) rot=(0,0,1;0rad)
  Radius = 1.5
FEATURE [Part::Cylinder] Cylinder594  label="Válec594"
  Angle = 360
  AttacherType = Attacher::AttachEngine3D
  Height = 40
  Placement = pos=(0,83,15) rot=(0,0,1;0rad)
  Radius = 2.65
FEATURE [Part::Cylinder] Cylinder597  label="Válec597"
  Angle = 360
  AttacherType = Attacher::AttachEngine3D
  Height = 40
  Placement = pos=(0,83,15) rot=(0,0,1;0rad)
  Radius = 2.65
FEATURE [Part::Box] Box001  label="Krychle001"
  AttacherType = Attacher::AttachEngine3D
  Height = 20
  Length = 6
  Placement = pos=(-14,80,38) rot=(0,0,1;0rad)
  Width = 6
FEATURE [Part::Cylinder] Cylinder596  label="Válec596"
  Angle = 360
  AttacherType = Attacher::AttachEngine3D
  Height = 30
  Placement = pos=(11,83,15) rot=(0,0,1;0rad)
  Radius = 1.5
FEATURE [Part::FeaturePython] wormgear027  # WARN: FeaturePython — macro-defined, semantics opaque (R4)
  AttacherType = Attacher::AttachEngine3D
  Placement = pos=(0,83,32) rot=(0,0,1;0.069813rad)
  beta = 33.1113
  clearance = 0.25
  diameter = 46
  head = 0
  height = 5
  module = 1
  pressure_angle = 20
  reverse_pitch = false
  teeth = 30
  version = 0.0.3
FEATURE [Part::FeaturePython] wormgear026  # WARN: FeaturePython — macro-defined, semantics opaque (R4)
  AttacherType = Attacher::AttachEngine3D
  Placement = pos=(0,83,37) rot=(0,0,1;0.191986rad)
  beta = 33.1113
  clearance = 0.25
  diameter = 46
  head = 0
  height = 5
  module = 1
  pressure_angle = 20
  reverse_pitch = true
  teeth = 30
  version = 0.0.3
FEATURE [Part::Cylinder] Cylinder658  label="Válec658"
  Angle = 360
  AttacherType = Attacher::AttachEngine3D
  Height = 30
  Placement = pos=(0,72,232) rot=(0,0,1;0rad)
  Radius = 1.5
FEATURE [Part::Cylinder] Cylinder659  label="Válec659"
  Angle = 360
  AttacherType = Attacher::AttachEngine3D
  Height = 30
  Placement = pos=(-11,83,232) rot=(0,0,1;0rad)
  Radius = 1.5
FEATURE [Part::Cylinder] Cylinder660  label="Válec660"
  Angle = 360
  AttacherType = Attacher::AttachEngine3D
  Height = 30
  Placement = pos=(11,83,232) rot=(0,0,1;0rad)
  Radius = 1.5
FEATURE [Part::Cylinder] Cylinder661  label="Válec661"
  Angle = 360
  AttacherType = Attacher::AttachEngine3D
  Height = 3
  Placement = pos=(0,72,232) rot=(0,0,1;0rad)
  Radius = 3
FEATURE [Part::Cylinder] Cylinder662  label="Válec662"
  Angle = 360
  AttacherType = Attacher::AttachEngine3D
  Height = 30
  Placement = pos=(0,72,232) rot=(0,0,1;0rad)
  Radius = 1.5
FEATURE [Part::Cylinder] Cylinder663  label="Válec663"
  Angle = 360
  AttacherType = Attacher::AttachEngine3D
  Height = 30
  Placement = pos=(0,94,232) rot=(0,0,1;0rad)
  Radius = 1.5
FEATURE [Part::Compound] Compound363
  Links = -> [Cylinder659,Cylinder660,Cylinder662,Cylinder663]
FEATURE [Part::FeaturePython] bevelgear011  # WARN: FeaturePython — macro-defined, semantics opaque (R4)
  AttacherType = Attacher::AttachEngine3D
  Placement = pos=(0,0,-254.4) rot=(1,0,0;3.14159rad)
  backlash = 0
  beta = 12
  clearance = 0.1
  height = 16
  module = 0.1
  numpoints = 6
  pitch_angle = 72.71
  pressure_angle = 21
  reset_origin = true
  teeth = 36
  version = 0.0.3
FEATURE [Part::Compound] Compound364
  Links = -> [Box,Box001,Box002,Box003]
FEATURE [Part::Compound] Compound365
  Links = -> [Cylinder592,Cylinder593,Cylinder598,Cylinder599]
FEATURE [Part::Cut] Cut230
  Base = -> wormgear027
  Tool = -> Compound365
FEATURE [Part::Cut] Cut231
  Base = -> Cut230
  Tool = -> Cylinder594
FEATURE [Part::Cylinder] Cylinder  label="Válec"
  Angle = 360
  AttacherType = Attacher::AttachEngine3D
  Height = 10
  Placement = pos=(0,83,232) rot=(0,0,1;0rad)
  Radius = 25
FEATURE [PartDesign::Body] Body012
  Group = -> [Revolution014,Sketch014]
  Origin = -> Origin012
  Placement = pos=(0,0,-199.6) rot=(0,0,1;0rad)
  Tip = -> Revolution014
FEATURE [Part::Common] Common002
  Base = -> Body012
  Placement = pos=(0,83,507) rot=(0,0,1;0rad)
  Tool = -> bevelgear011
FEATURE [Part::Cylinder] Cylinder664  label="Válec664"
  Angle = 360
  AttacherType = Attacher::AttachEngine3D
  Height = 3
  Placement = pos=(11,83,232) rot=(0,0,1;0rad)
  Radius = 3
FEATURE [Part::Cylinder] Cylinder665  label="Válec665"
  Angle = 360
  AttacherType = Attacher::AttachEngine3D
  Height = 10
  Placement = pos=(0,83,242) rot=(0,0,1;0rad)
  Radius = 15.1
FEATURE [Part::Cylinder] Cylinder666  label="Válec666"
  Angle = 360
  AttacherType = Attacher::AttachEngine3D
  Height = 3
  Placement = pos=(-11,83,232) rot=(0,0,1;0rad)
  Radius = 3
FEATURE [Part::Cylinder] Cylinder667  label="Válec667"
  Angle = 360
  AttacherType = Attacher::AttachEngine3D
  Height = 30
  Placement = pos=(-11,83,232) rot=(0,0,1;0rad)
  Radius = 1.5
FEATURE [Part::Cylinder] Cylinder668  label="Válec668"
  Angle = 360
  AttacherType = Attacher::AttachEngine3D
  Height = 3
  Placement = pos=(0,94,232) rot=(0,0,1;0rad)
  Radius = 3
FEATURE [Part::Compound] Compound362
  Links = -> [Cylinder666,Cylinder664,Cylinder661,Cylinder668]
  Placement = pos=(0,0,17) rot=(0,0,1;0rad)
FEATURE [Part::Cylinder] Cylinder669  label="Válec669"
  Angle = 360
  AttacherType = Attacher::AttachEngine3D
  Height = 17
  Placement = pos=(0,83,252) rot=(0,0,1;0rad)
  Radius = 8
FEATURE [Part::Cylinder] Cylinder670  label="Válec670"
  Angle = 360
  AttacherType = Attacher::AttachEngine3D
  Height = 40
  Placement = pos=(0,83,232) rot=(0,0,1;0rad)
  Radius = 2.65
FEATURE [Part::Cut] Cut268
  Base = -> Cylinder669
  Tool = -> Cylinder670
FEATURE [Part::Cylinder] Cylinder671  label="Válec671"
  Angle = 360
  AttacherType = Attacher::AttachEngine3D
  Height = 30
  Placement = pos=(0,94,232) rot=(0,0,1;0rad)
  Radius = 1.5
FEATURE [Part::Cylinder] Cylinder672  label="Válec672"
  Angle = 360
  AttacherType = Attacher::AttachEngine3D
  Height = 30
  Placement = pos=(0,83,232) rot=(0,0,1;0rad)
  Radius = 2.65
FEATURE [Part::Cylinder] Cylinder673  label="Válec673"
  Angle = 360
  AttacherType = Attacher::AttachEngine3D
  Height = 30
  Placement = pos=(11,83,232) rot=(0,0,1;0rad)
  Radius = 1.5
FEATURE [Part::Compound] Compound361
  Links = -> [Cylinder667,Cylinder673,Cylinder658,Cylinder671]
FEATURE [Part::Cut] Cut269
  Base = -> Cylinder665
  Tool = -> Compound361
FEATURE [Part::Cut] Cut270
  Base = -> Cut269
  Tool = -> Compound362
FEATURE [Part::Cut] Cut267
  Base = -> Cut270
  Tool = -> Cylinder672
FEATURE [Part::Cut] Cut271
  Base = -> Common002
  Tool = -> Compound363
FEATURE [Part::Cut] Cut228
  Base = -> Cut271
  Tool = -> Cylinder
FEATURE [Part::Compound] Compound367
  Links = -> [Cylinder591,Cylinder596,Cylinder600,Cylinder595]
FEATURE [Part::Cut] Cut229
  Base = -> wormgear026
  Tool = -> Compound367
FEATURE [Part::Cut] Cut232
  Base = -> Cut229
  Tool = -> Cylinder597
FEATURE [Part::Cut] Cut233
  Base = -> Cut232
  Tool = -> Compound364
FEATURE [Part::Compound] Compound368  label="bazovina-prevod-B"
  Links = -> [Cut231,Cut233]
  Placement = pos=(0,0,200) rot=(0,0,1;0rad)
FEATURE [Part::Compound] Compound369
  Links = -> [Cut228,Cut267,Cut268]
FEATURE [Part::Compound] Compound366  label="Base_rear-gear-large"
  Links = -> [Compound369,Compound368]
  Placement = pos=(0,0,-205) rot=(0,0,1;0rad)
FEATURE [Sketcher::SketchObject] Sketch015
  FullyConstrained = false
  MapMode = 5
  Placement = pos=(0,0,0) rot=(1,0,0;1.5708rad)
  Support = -> [XZ_Plane016]
  sketch-geometry (29):
    g0: LineSegment StartX=0 StartY=-63.1814 StartZ=0 EndX=22.5 EndY=-63.1814 EndZ=0
    g1: LineSegment StartX=22.5 StartY=-63.1814 StartZ=0 EndX=22.5 EndY=-67.1814 EndZ=0
    g2: LineSegment StartX=22.5 StartY=-67.1814 StartZ=0 EndX=0 EndY=-67.1814 EndZ=0
    g3: LineSegment StartX=0 StartY=-67.1814 StartZ=0 EndX=0 EndY=-63.1814 EndZ=0
    g4: LineSegment StartX=22.5 StartY=-63.1814 StartZ=0 EndX=26.5 EndY=-63.1814 EndZ=0
    g5: LineSegment StartX=26.5 StartY=-63.1814 StartZ=0 EndX=26.5 EndY=-58.1814 EndZ=0
    g6: LineSegment StartX=26.5 StartY=-58.1814 StartZ=0 EndX=22.5 EndY=-58.1814 EndZ=0
    g7: LineSegment StartX=22.5 StartY=-58.1814 StartZ=0 EndX=22.5 EndY=-63.1814 EndZ=0
    g8: LineSegment StartX=22.5 StartY=-63.1814 StartZ=0 EndX=0 EndY=-63.1814 EndZ=0
    g9: LineSegment StartX=0 StartY=-63.1814 StartZ=0 EndX=0 EndY=-56.1814 EndZ=0
    g10: LineSegment StartX=0 StartY=-56.1814 StartZ=0 EndX=22.5 EndY=-56.1814 EndZ=0
    g11: LineSegment StartX=22.5 StartY=-56.1814 StartZ=0 EndX=22.5 EndY=-63.1814 EndZ=0
    g12: LineSegment StartX=0 StartY=-56.1814 StartZ=0 EndX=22.5 EndY=-63.1814 EndZ=0
    g13: LineSegment StartX=22.5 StartY=-63.1814 StartZ=0 EndX=21.9059 EndY=-65.0911 EndZ=0
    g14: LineSegment StartX=22.5 StartY=-63.1814 StartZ=0 EndX=23.0941 EndY=-61.2717 EndZ=0
    g15: LineSegment StartX=23.0941 StartY=-61.2717 StartZ=0 EndX=0 EndY=-56.1814 EndZ=0
    g16: LineSegment StartX=21.9059 StartY=-65.0911 StartZ=0 EndX=0 EndY=-56.1814 EndZ=0
    g17: LineSegment StartX=23.0941 StartY=-61.2717 StartZ=0 EndX=15.2817 EndY=-59.5497 EndZ=0
    g18: LineSegment StartX=15.2817 StartY=-59.5497 StartZ=0 EndX=14.1518 EndY=-63.1814 EndZ=0
    g19: LineSegment StartX=15.2817 StartY=-56.1814 StartZ=0 EndX=15.2817 EndY=-59.5497 EndZ=0
    g20: LineSegment StartX=21.9059 StartY=-65.0911 StartZ=0 EndX=21.9059 EndY=-67.1814 EndZ=0
    g21: LineSegment StartX=23.0941 StartY=-61.2717 StartZ=0 EndX=26.5 EndY=-61.2717 EndZ=0
    g22: LineSegment StartX=21.9059 StartY=-67.1814 StartZ=0 EndX=21.9059 EndY=-65.0911 EndZ=0
    g23: LineSegment StartX=21.9059 StartY=-65.0911 StartZ=0 EndX=23.0941 EndY=-61.2717 EndZ=0
    g24: LineSegment StartX=23.0941 StartY=-61.2717 StartZ=0 EndX=15.2817 EndY=-59.5497 EndZ=0
    g25: LineSegment StartX=15.2817 StartY=-59.5497 StartZ=0 EndX=14.1518 EndY=-63.1814 EndZ=0
    g26: LineSegment StartX=14.1518 StartY=-63.1814 StartZ=0 EndX=0 EndY=-63.1814 EndZ=0
    g27: LineSegment StartX=0 StartY=-63.1814 StartZ=0 EndX=0 EndY=-67.1814 EndZ=0
    g28: LineSegment StartX=0 StartY=-67.1814 StartZ=0 EndX=21.9059 EndY=-67.1814 EndZ=0
  constraints (77):
    c: Coincident(g0,g1)
    c: Coincident(g1,g2)
    c: Coincident(g2,g3)
    c: Coincident(g3,g0)
    c: Horizontal(g0)
    c: Horizontal(g2)
    c: Vertical(g1)
    c: Vertical(g3)
    c: PointOnObject(g0,g-2)
    c: Distance(g0) = 22.5
    c: Distance(g1) = 4
    c: Coincident(g4,g5)
    c: Coincident(g5,g6)
    c: Coincident(g6,g7)
    c: Coincident(g7,g4)
    c: Horizontal(g4)
    c: Horizontal(g6)
    c: Vertical(g5)
    c: Vertical(g7)
    c: Coincident(g4,g0)
    c: Distance(g7) = 5
    c: Distance(g6) = 4
    c: Coincident(g8,g9)
    c: Coincident(g9,g10)
    c: Coincident(g10,g11)
    c: Coincident(g11,g8)
    c: Horizontal(g8)
    c: Horizontal(g10)
    c: Vertical(g9)
    c: Vertical(g11)
    c: Coincident(g8,g0)
    c: PointOnObject(g9,g-2)
    c: Distance(g9) = 7
    c: Coincident(g12,g9)
    c: Coincident(g12,g0)
    c: Coincident(g13,g0)
    c: Perpendicular(g13,g12)
    c: Distance(g13) = 2
    c: Coincident(g14,g0)
    c: Distance(g14) = 2
    c: Perpendicular(g14,g12)
    c: Coincident(g15,g14)
    c: Coincident(g15,g9)
    c: Coincident(g16,g13)
    c: Coincident(g16,g9)
    c: Coincident(g17,g14)
    c: PointOnObject(g17,g15)
    c: Distance(g17) = 8
    c: Coincident(g18,g17)
    c: PointOnObject(g18,g0)
    c: Perpendicular(g18,g12)
    c: PointOnObject(g19,g10)
    c: Coincident(g19,g17)
    c: Vertical(g19)
    c: Coincident(g20,g13)
    c: PointOnObject(g20,g2)
    c: Vertical(g20)
    c: Coincident(g21,g14)
    c: PointOnObject(g21,g5)
    c: Horizontal(g21)
    c: Angle(g15,g10) = 0.216946
    c: Angle(g12,g10) = 0.301619
    c: Angle(g9,g12) = 1.26918
    c: Coincident(g22,g20)
    c: Coincident(g22,g13)
    c: Coincident(g22,g23)
    c: Coincident(g23,g14)
    c: Coincident(g23,g24)
    c: Coincident(g24,g17)
    c: Coincident(g24,g25)
    c: Coincident(g25,g18)
    c: Coincident(g26,g25)
    c: Coincident(g26,g0)
    c: Coincident(g27,g26)
    c: Coincident(g27,g2)
    c: Coincident(g28,g27)
    c: Coincident(g28,g22)
FEATURE [Part::Cylinder] Cylinder674  label="Válec674"
  Angle = 360
  AttacherType = Attacher::AttachEngine3D
  Height = 30
  Placement = pos=(0,72,15) rot=(0,0,1;0rad)
  Radius = 1.5
FEATURE [Part::Box] Box257  label="Krychle257"
  AttacherType = Attacher::AttachEngine3D
  Height = 20
  Length = 6
  Placement = pos=(-3,91,38) rot=(0,0,1;0rad)
  Width = 6
FEATURE [Part::Cylinder] Cylinder675  label="Válec675"
  Angle = 360
  AttacherType = Attacher::AttachEngine3D
  Height = 30
  Placement = pos=(0,72,15) rot=(0,0,1;0rad)
  Radius = 1.5
FEATURE [Part::Cylinder] Cylinder676  label="Válec676"
  Angle = 360
  AttacherType = Attacher::AttachEngine3D
  Height = 30
  Placement = pos=(0,94,15) rot=(0,0,1;0rad)
  Radius = 1.5
FEATURE [Part::Cylinder] Cylinder677  label="Válec677"
  Angle = 360
  AttacherType = Attacher::AttachEngine3D
  Height = 30
  Placement = pos=(11,83,15) rot=(0,0,1;0rad)
  Radius = 1.5
FEATURE [Part::Cylinder] Cylinder678  label="Válec678"
  Angle = 360
  AttacherType = Attacher::AttachEngine3D
  Height = 30
  Placement = pos=(0,94,15) rot=(0,0,1;0rad)
  Radius = 1.5
FEATURE [Part::Box] Box258  label="Krychle258"
  AttacherType = Attacher::AttachEngine3D
  Height = 20
  Length = 6
  Placement = pos=(8,80,38) rot=(0,0,1;0rad)
  Width = 6
FEATURE [Part::Cylinder] Cylinder679  label="Válec679"
  Angle = 360
  AttacherType = Attacher::AttachEngine3D
  Height = 30
  Placement = pos=(-11,83,15) rot=(0,0,1;0rad)
  Radius = 1.5
FEATURE [Part::Box] Box259  label="Krychle259"
  AttacherType = Attacher::AttachEngine3D
  Height = 20
  Length = 6
  Placement = pos=(-3,69,38) rot=(0,0,1;0rad)
  Width = 6
FEATURE [PartDesign::Revolution] Revolution015
  Angle = 360
  Axis = (0,-9e-16,4)
  Base = (0,1.49e-14,-67.1814)
  Placement = pos=(0,0,0) rot=(1,0,0;1.5708rad)
  Profile = -> Sketch015
  ReferenceAxis = -> Sketch015 [Axis3]
  Reversed = true
FEATURE [PartDesign::Body] Body013
  Group = -> [Revolution015,Sketch015]
  Origin = -> Origin013
  Placement = pos=(0,0,-199.6) rot=(0,0,1;0rad)
  Tip = -> Revolution015
FEATURE [Part::Cylinder] Cylinder680  label="Válec680"
  Angle = 360
  AttacherType = Attacher::AttachEngine3D
  Height = 40
  Placement = pos=(0,83,15) rot=(0,0,1;0rad)
  Radius = 2.65
FEATURE [Part::Cylinder] Cylinder681  label="Válec681"
  Angle = 360
  AttacherType = Attacher::AttachEngine3D
  Height = 30
  Placement = pos=(-11,83,15) rot=(0,0,1;0rad)
  Radius = 1.5
FEATURE [Part::Cylinder] Cylinder682  label="Válec682"
  Angle = 360
  AttacherType = Attacher::AttachEngine3D
  Height = 40
  Placement = pos=(0,83,15) rot=(0,0,1;0rad)
  Radius = 2.65
FEATURE [Part::Cylinder] Cylinder683  label="Válec683"
  Angle = 360
  AttacherType = Attacher::AttachEngine3D
  Height = 30
  Placement = pos=(11,83,15) rot=(0,0,1;0rad)
  Radius = 1.5
FEATURE [Part::Box] Box260  label="Krychle260"
  AttacherType = Attacher::AttachEngine3D
  Height = 20
  Length = 6
  Placement = pos=(-14,80,38) rot=(0,0,1;0rad)
  Width = 6
FEATURE [Part::Cylinder] Cylinder684  label="Válec684"
  Angle = 360
  AttacherType = Attacher::AttachEngine3D
  Height = 30
  Placement = pos=(0,72,232) rot=(0,0,1;0rad)
  Radius = 1.5
FEATURE [Part::Cylinder] Cylinder685  label="Válec685"
  Angle = 360
  AttacherType = Attacher::AttachEngine3D
  Height = 30
  Placement = pos=(-11,83,232) rot=(0,0,1;0rad)
  Radius = 1.5
FEATURE [Part::Cylinder] Cylinder686  label="Válec686"
  Angle = 360
  AttacherType = Attacher::AttachEngine3D
  Height = 30
  Placement = pos=(11,83,232) rot=(0,0,1;0rad)
  Radius = 1.5
FEATURE [Part::FeaturePython] wormgear028  # WARN: FeaturePython — macro-defined, semantics opaque (R4)
  AttacherType = Attacher::AttachEngine3D
  Placement = pos=(0,83,32) rot=(0,0,1;0.069813rad)
  beta = 33.1113
  clearance = 0.25
  diameter = 46
  head = 0
  height = 5
  module = 1
  pressure_angle = 20
  reverse_pitch = false
  teeth = 30
  version = 0.0.3
FEATURE [Part::FeaturePython] wormgear029  # WARN: FeaturePython — macro-defined, semantics opaque (R4)
  AttacherType = Attacher::AttachEngine3D
  Placement = pos=(0,83,37) rot=(0,0,1;0.191986rad)
  beta = 33.1113
  clearance = 0.25
  diameter = 46
  head = 0
  height = 5
  module = 1
  pressure_angle = 20
  reverse_pitch = true
  teeth = 30
  version = 0.0.3
FEATURE [Part::Cylinder] Cylinder687  label="Válec687"
  Angle = 360
  AttacherType = Attacher::AttachEngine3D
  Height = 3
  Placement = pos=(-11,83,232) rot=(0,0,1;0rad)
  Radius = 3
FEATURE [Part::Cylinder] Cylinder688  label="Válec688"
  Angle = 360
  AttacherType = Attacher::AttachEngine3D
  Height = 30
  Placement = pos=(-11,83,232) rot=(0,0,1;0rad)
  Radius = 1.5
FEATURE [Part::Cylinder] Cylinder689  label="Válec689"
  Angle = 360
  AttacherType = Attacher::AttachEngine3D
  Height = 30
  Placement = pos=(0,72,232) rot=(0,0,1;0rad)
  Radius = 1.5
FEATURE [Part::Cylinder] Cylinder690  label="Válec690"
  Angle = 360
  AttacherType = Attacher::AttachEngine3D
  Height = 3
  Placement = pos=(0,72,232) rot=(0,0,1;0rad)
  Radius = 3
FEATURE [Part::Cylinder] Cylinder691  label="Válec691"
  Angle = 360
  AttacherType = Attacher::AttachEngine3D
  Height = 30
  Placement = pos=(0,94,232) rot=(0,0,1;0rad)
  Radius = 1.5
FEATURE [Part::Compound] Compound372
  Links = -> [Cylinder685,Cylinder686,Cylinder689,Cylinder691]
FEATURE [Part::Cylinder] Cylinder692  label="Válec692"
  Angle = 360
  AttacherType = Attacher::AttachEngine3D
  Height = 10
  Placement = pos=(0,83,232) rot=(0,0,1;0rad)
  Radius = 25
FEATURE [Part::Cylinder] Cylinder693  label="Válec693"
  Angle = 360
  AttacherType = Attacher::AttachEngine3D
  Height = 3
  Placement = pos=(11,83,232) rot=(0,0,1;0rad)
  Radius = 3
FEATURE [Part::Cylinder] Cylinder694  label="Válec694"
  Angle = 360
  AttacherType = Attacher::AttachEngine3D
  Height = 10
  Placement = pos=(0,83,242) rot=(0,0,1;0rad)
  Radius = 15.1
FEATURE [Part::FeaturePython] bevelgear012  # WARN: FeaturePython — macro-defined, semantics opaque (R4)
  AttacherType = Attacher::AttachEngine3D
  Placement = pos=(0,0,-254.4) rot=(1,0,0;3.14159rad)
  backlash = 0
  beta = 12
  clearance = 0.1
  height = 16
  module = 0.1
  numpoints = 6
  pitch_angle = 72.71
  pressure_angle = 21
  reset_origin = true
  teeth = 36
  version = 0.0.3
FEATURE [Part::Common] Common003
  Base = -> Body013
  Placement = pos=(0,83,507) rot=(0,0,1;0rad)
  Tool = -> bevelgear012
FEATURE [Part::Cut] Cut276
  Base = -> Common003
  Tool = -> Compound372
FEATURE [Part::Cut] Cut280
  Base = -> Cut276
  Tool = -> Cylinder692
FEATURE [Part::Compound] Compound373
  Links = -> [Box258,Box260,Box259,Box257]
FEATURE [Part::Compound] Compound374
  Links = -> [Cylinder681,Cylinder677,Cylinder675,Cylinder676]
FEATURE [Part::Cut] Cut278
  Base = -> wormgear028
  Tool = -> Compound374
FEATURE [Part::Cut] Cut273
  Base = -> Cut278
  Tool = -> Cylinder680
FEATURE [Part::Cylinder] Cylinder695  label="Válec695"
  Angle = 360
  AttacherType = Attacher::AttachEngine3D
  Height = 30
  Placement = pos=(0,83,232) rot=(0,0,1;0rad)
  Radius = 2.65
FEATURE [Part::Cylinder] Cylinder696  label="Válec696"
  Angle = 360
  AttacherType = Attacher::AttachEngine3D
  Height = 17
  Placement = pos=(0,83,252) rot=(0,0,1;0rad)
  Radius = 8
FEATURE [Part::Cylinder] Cylinder697  label="Válec697"
  Angle = 360
  AttacherType = Attacher::AttachEngine3D
  Height = 40
  Placement = pos=(0,83,232) rot=(0,0,1;0rad)
  Radius = 2.65
FEATURE [Part::Cut] Cut275
  Base = -> Cylinder696
  Tool = -> Cylinder697
FEATURE [Part::Cylinder] Cylinder698  label="Válec698"
  Angle = 360
  AttacherType = Attacher::AttachEngine3D
  Height = 3
  Placement = pos=(0,94,232) rot=(0,0,1;0rad)
  Radius = 3
FEATURE [Part::Compound] Compound371
  Links = -> [Cylinder687,Cylinder693,Cylinder690,Cylinder698]
  Placement = pos=(0,0,17) rot=(0,0,1;0rad)
FEATURE [Part::Cylinder] Cylinder699  label="Válec699"
  Angle = 360
  AttacherType = Attacher::AttachEngine3D
  Height = 30
  Placement = pos=(11,83,232) rot=(0,0,1;0rad)
  Radius = 1.5
FEATURE [Part::Cylinder] Cylinder700  label="Válec700"
  Angle = 360
  AttacherType = Attacher::AttachEngine3D
  Height = 30
  Placement = pos=(0,94,232) rot=(0,0,1;0rad)
  Radius = 1.5
FEATURE [Part::Compound] Compound370
  Links = -> [Cylinder688,Cylinder699,Cylinder684,Cylinder700]
FEATURE [Part::Cut] Cut274
  Base = -> Cylinder694
  Tool = -> Compound370
FEATURE [Part::Cut] Cut277
  Base = -> Cut274
  Tool = -> Compound371
FEATURE [Part::Cut] Cut279
  Base = -> Cut277
  Tool = -> Cylinder695
FEATURE [Part::Compound] Compound376
  Links = -> [Cylinder679,Cylinder683,Cylinder674,Cylinder678]
FEATURE [Part::Cut] Cut272
  Base = -> wormgear029
  Tool = -> Compound376
FEATURE [Part::Cut] Cut281
  Base = -> Cut272
  Tool = -> Cylinder682
FEATURE [Part::Cut] Cut282
  Base = -> Cut281
  Tool = -> Compound373
FEATURE [Part::FeaturePython] wormgear030  # WARN: FeaturePython — macro-defined, semantics opaque (R4)
  AttacherType = Attacher::AttachEngine3D
  Placement = pos=(0,83,32) rot=(0,0,1;0.106465rad)
  beta = 33.1113
  clearance = 0.25
  diameter = 46
  head = 0
  height = 5
  module = 1
  pressure_angle = 20
  reverse_pitch = true
  teeth = 30
  version = 0.0.3
FEATURE [Part::FeaturePython] wormgear031  # WARN: FeaturePython — macro-defined, semantics opaque (R4)
  AttacherType = Attacher::AttachEngine3D
  Placement = pos=(0,83,37) rot=(0,0,1;0.191986rad)
  beta = 33.1113
  clearance = 0.25
  diameter = 46
  head = 0
  height = 5
  module = 1
  pressure_angle = 20
  reverse_pitch = false
  teeth = 30
  version = 0.0.3
FEATURE [Part::Cylinder] Cylinder701  label="Válec701"
  Angle = 360
  AttacherType = Attacher::AttachEngine3D
  Height = 40
  Placement = pos=(0,83,15) rot=(0,0,1;0rad)
  Radius = 2.65
FEATURE [Part::Cylinder] Cylinder702  label="Válec702"
  Angle = 360
  AttacherType = Attacher::AttachEngine3D
  Height = 40
  Placement = pos=(0,83,15) rot=(0,0,1;0rad)
  Radius = 2.65
FEATURE [Part::Cut] Cut
  Base = -> wormgear030
  Tool = -> Cylinder701
FEATURE [Part::Cut] Cut283
  Base = -> wormgear031
  Tool = -> Cylinder702
FEATURE [Part::Compound] Compound379
  Links = -> [Cut,Cut283]
  Placement = pos=(0,0,200) rot=(0,0,1;0rad)
FEATURE [Part::Cylinder] Cylinder703  label="Válec703"
  Angle = 360
  AttacherType = Attacher::AttachEngine3D
  Height = 10
  Placement = pos=(0,83,242) rot=(0,0,1;0rad)
  Radius = 15.1
FEATURE [Part::Cylinder] Cylinder704  label="Válec704"
  Angle = 360
  AttacherType = Attacher::AttachEngine3D
  Height = 30
  Placement = pos=(0,83,232) rot=(0,0,1;0rad)
  Radius = 2.65
FEATURE [Part::Cut] Cut284
  Base = -> Cylinder703
  Tool = -> Cylinder704
FEATURE [Part::FeaturePython] bevelgear013  # WARN: FeaturePython — macro-defined, semantics opaque (R4)
  AttacherType = Attacher::AttachEngine3D
  Placement = pos=(0,0,-254.4) rot=(1,0,0;3.14159rad)
  backlash = 0
  beta = 12
  clearance = 0.1
  height = 16
  module = 0.1
  numpoints = 6
  pitch_angle = 72.71
  pressure_angle = 21
  reset_origin = true
  teeth = 36
  version = 0.0.3
FEATURE [Part::Cylinder] Cylinder705  label="Válec705"
  Angle = 360
  AttacherType = Attacher::AttachEngine3D
  Height = 10
  Placement = pos=(0,83,232) rot=(0,0,1;0rad)
  Radius = 25
FEATURE [Sketcher::SketchObject] Sketch016
  FullyConstrained = false
  MapMode = 5
  Placement = pos=(0,0,0) rot=(1,0,0;1.5708rad)
  Support = -> [XZ_Plane017]
  sketch-geometry (29):
    g0: LineSegment StartX=0 StartY=-63.1814 StartZ=0 EndX=22.5 EndY=-63.1814 EndZ=0
    g1: LineSegment StartX=22.5 StartY=-63.1814 StartZ=0 EndX=22.5 EndY=-67.1814 EndZ=0
    g2: LineSegment StartX=22.5 StartY=-67.1814 StartZ=0 EndX=0 EndY=-67.1814 EndZ=0
    g3: LineSegment StartX=0 StartY=-67.1814 StartZ=0 EndX=0 EndY=-63.1814 EndZ=0
    g4: LineSegment StartX=22.5 StartY=-63.1814 StartZ=0 EndX=26.5 EndY=-63.1814 EndZ=0
    g5: LineSegment StartX=26.5 StartY=-63.1814 StartZ=0 EndX=26.5 EndY=-58.1814 EndZ=0
    g6: LineSegment StartX=26.5 StartY=-58.1814 StartZ=0 EndX=22.5 EndY=-58.1814 EndZ=0
    g7: LineSegment StartX=22.5 StartY=-58.1814 StartZ=0 EndX=22.5 EndY=-63.1814 EndZ=0
    g8: LineSegment StartX=22.5 StartY=-63.1814 StartZ=0 EndX=0 EndY=-63.1814 EndZ=0
    g9: LineSegment StartX=0 StartY=-63.1814 StartZ=0 EndX=0 EndY=-56.1814 EndZ=0
    g10: LineSegment StartX=0 StartY=-56.1814 StartZ=0 EndX=22.5 EndY=-56.1814 EndZ=0
    g11: LineSegment StartX=22.5 StartY=-56.1814 StartZ=0 EndX=22.5 EndY=-63.1814 EndZ=0
    g12: LineSegment StartX=0 StartY=-56.1814 StartZ=0 EndX=22.5 EndY=-63.1814 EndZ=0
    g13: LineSegment StartX=22.5 StartY=-63.1814 StartZ=0 EndX=21.9059 EndY=-65.0911 EndZ=0
    g14: LineSegment StartX=22.5 StartY=-63.1814 StartZ=0 EndX=23.0941 EndY=-61.2717 EndZ=0
    g15: LineSegment StartX=23.0941 StartY=-61.2717 StartZ=0 EndX=0 EndY=-56.1814 EndZ=0
    g16: LineSegment StartX=21.9059 StartY=-65.0911 StartZ=0 EndX=0 EndY=-56.1814 EndZ=0
    g17: LineSegment StartX=23.0941 StartY=-61.2717 StartZ=0 EndX=15.2817 EndY=-59.5497 EndZ=0
    g18: LineSegment StartX=15.2817 StartY=-59.5497 StartZ=0 EndX=14.1518 EndY=-63.1814 EndZ=0
    g19: LineSegment StartX=15.2817 StartY=-56.1814 StartZ=0 EndX=15.2817 EndY=-59.5497 EndZ=0
    g20: LineSegment StartX=21.9059 StartY=-65.0911 StartZ=0 EndX=21.9059 EndY=-67.1814 EndZ=0
    g21: LineSegment StartX=23.0941 StartY=-61.2717 StartZ=0 EndX=26.5 EndY=-61.2717 EndZ=0
    g22: LineSegment StartX=21.9059 StartY=-67.1814 StartZ=0 EndX=21.9059 EndY=-65.0911 EndZ=0
    g23: LineSegment StartX=21.9059 StartY=-65.0911 StartZ=0 EndX=23.0941 EndY=-61.2717 EndZ=0
    g24: LineSegment StartX=23.0941 StartY=-61.2717 StartZ=0 EndX=15.2817 EndY=-59.5497 EndZ=0
    g25: LineSegment StartX=15.2817 StartY=-59.5497 StartZ=0 EndX=14.1518 EndY=-63.1814 EndZ=0
    g26: LineSegment StartX=14.1518 StartY=-63.1814 StartZ=0 EndX=0 EndY=-63.1814 EndZ=0
    g27: LineSegment StartX=0 StartY=-63.1814 StartZ=0 EndX=0 EndY=-67.1814 EndZ=0
    g28: LineSegment StartX=0 StartY=-67.1814 StartZ=0 EndX=21.9059 EndY=-67.1814 EndZ=0
  constraints (77):
    c: Coincident(g0,g1)
    c: Coincident(g1,g2)
    c: Coincident(g2,g3)
    c: Coincident(g3,g0)
    c: Horizontal(g0)
    c: Horizontal(g2)
    c: Vertical(g1)
    c: Vertical(g3)
    c: PointOnObject(g0,g-2)
    c: Distance(g0) = 22.5
    c: Distance(g1) = 4
    c: Coincident(g4,g5)
    c: Coincident(g5,g6)
    c: Coincident(g6,g7)
    c: Coincident(g7,g4)
    c: Horizontal(g4)
    c: Horizontal(g6)
    c: Vertical(g5)
    c: Vertical(g7)
    c: Coincident(g4,g0)
    c: Distance(g7) = 5
    c: Distance(g6) = 4
    c: Coincident(g8,g9)
    c: Coincident(g9,g10)
    c: Coincident(g10,g11)
    c: Coincident(g11,g8)
    c: Horizontal(g8)
    c: Horizontal(g10)
    c: Vertical(g9)
    c: Vertical(g11)
    c: Coincident(g8,g0)
    c: PointOnObject(g9,g-2)
    c: Distance(g9) = 7
    c: Coincident(g12,g9)
    c: Coincident(g12,g0)
    c: Coincident(g13,g0)
    c: Perpendicular(g13,g12)
    c: Distance(g13) = 2
    c: Coincident(g14,g0)
    c: Distance(g14) = 2
    c: Perpendicular(g14,g12)
    c: Coincident(g15,g14)
    c: Coincident(g15,g9)
    c: Coincident(g16,g13)
    c: Coincident(g16,g9)
    c: Coincident(g17,g14)
    c: PointOnObject(g17,g15)
    c: Distance(g17) = 8
    c: Coincident(g18,g17)
    c: PointOnObject(g18,g0)
    c: Perpendicular(g18,g12)
    c: PointOnObject(g19,g10)
    c: Coincident(g19,g17)
    c: Vertical(g19)
    c: Coincident(g20,g13)
    c: PointOnObject(g20,g2)
    c: Vertical(g20)
    c: Coincident(g21,g14)
    c: PointOnObject(g21,g5)
    c: Horizontal(g21)
    c: Angle(g15,g10) = 0.216946
    c: Angle(g12,g10) = 0.301619
    c: Angle(g9,g12) = 1.26918
    c: Coincident(g22,g20)
    c: Coincident(g22,g13)
    c: Coincident(g22,g23)
    c: Coincident(g23,g14)
    c: Coincident(g23,g24)
    c: Coincident(g24,g17)
    c: Coincident(g24,g25)
    c: Coincident(g25,g18)
    c: Coincident(g26,g25)
    c: Coincident(g26,g0)
    c: Coincident(g27,g26)
    c: Coincident(g27,g2)
    c: Coincident(g28,g27)
    c: Coincident(g28,g22)
FEATURE [PartDesign::Revolution] Revolution016
  Angle = 360
  Axis = (0,-9e-16,4)
  Base = (0,1.49e-14,-67.1814)
  Placement = pos=(0,0,0) rot=(1,0,0;1.5708rad)
  Profile = -> Sketch016
  ReferenceAxis = -> Sketch016 [Axis3]
  Reversed = true
FEATURE [PartDesign::Body] Body014
  Group = -> [Revolution016,Sketch016]
  Origin = -> Origin014
  Placement = pos=(0,0,-199.6) rot=(0,0,1;0rad)
  Tip = -> Revolution016
FEATURE [Part::Common] Common004
  Base = -> Body014
  Placement = pos=(0,83,507) rot=(0,0,1;0rad)
  Tool = -> bevelgear013
FEATURE [Part::Cut] Cut285
  Base = -> Common004
  Tool = -> Cylinder705
FEATURE [Part::Cylinder] Cylinder706  label="Válec706"
  Angle = 360
  AttacherType = Attacher::AttachEngine3D
  Height = 40
  Placement = pos=(0,83,220) rot=(0,0,1;0rad)
  Radius = 2.65
FEATURE [Part::Cut] Cut286
  Base = -> Cut285
  Tool = -> Cylinder706
FEATURE [Part::Compound] Compound380  label="Base_rear-gear-large-solid"
  Links = -> [Cut284,Cut286,Cut275,Compound379]
FEATURE [Part::Chamfer] Chamfer001  label="Base_rear-gear-small"
  Base = -> Compound032
  Edges = 1 edges r=1: [Edge339]
FEATURE [Mesh::Feature] Mesh001  label="Base_rear-gear-small (Meshed)"
FEATURE [Sketcher::SketchObject] Sketch017
  FullyConstrained = false
  MapMode = 5
  Placement = pos=(0,0,0) rot=(1,0,0;1.5708rad)
  Support = -> [XZ_Plane018]
  sketch-geometry (29):
    g0: LineSegment StartX=0 StartY=-63.1814 StartZ=0 EndX=22.5 EndY=-63.1814 EndZ=0
    g1: LineSegment StartX=22.5 StartY=-63.1814 StartZ=0 EndX=22.5 EndY=-67.1814 EndZ=0
    g2: LineSegment StartX=22.5 StartY=-67.1814 StartZ=0 EndX=0 EndY=-67.1814 EndZ=0
    g3: LineSegment StartX=0 StartY=-67.1814 StartZ=0 EndX=0 EndY=-63.1814 EndZ=0
    g4: LineSegment StartX=22.5 StartY=-63.1814 StartZ=0 EndX=26.5 EndY=-63.1814 EndZ=0
    g5: LineSegment StartX=26.5 StartY=-63.1814 StartZ=0 EndX=26.5 EndY=-58.1814 EndZ=0
    g6: LineSegment StartX=26.5 StartY=-58.1814 StartZ=0 EndX=22.5 EndY=-58.1814 EndZ=0
    g7: LineSegment StartX=22.5 StartY=-58.1814 StartZ=0 EndX=22.5 EndY=-63.1814 EndZ=0
    g8: LineSegment StartX=22.5 StartY=-63.1814 StartZ=0 EndX=0 EndY=-63.1814 EndZ=0
    g9: LineSegment StartX=0 StartY=-63.1814 StartZ=0 EndX=0 EndY=-56.1814 EndZ=0
    g10: LineSegment StartX=0 StartY=-56.1814 StartZ=0 EndX=22.5 EndY=-56.1814 EndZ=0
    g11: LineSegment StartX=22.5 StartY=-56.1814 StartZ=0 EndX=22.5 EndY=-63.1814 EndZ=0
    g12: LineSegment StartX=0 StartY=-56.1814 StartZ=0 EndX=22.5 EndY=-63.1814 EndZ=0
    g13: LineSegment StartX=22.5 StartY=-63.1814 StartZ=0 EndX=21.9059 EndY=-65.0911 EndZ=0
    g14: LineSegment StartX=22.5 StartY=-63.1814 StartZ=0 EndX=23.0941 EndY=-61.2717 EndZ=0
    g15: LineSegment StartX=23.0941 StartY=-61.2717 StartZ=0 EndX=0 EndY=-56.1814 EndZ=0
    g16: LineSegment StartX=21.9059 StartY=-65.0911 StartZ=0 EndX=0 EndY=-56.1814 EndZ=0
    g17: LineSegment StartX=23.0941 StartY=-61.2717 StartZ=0 EndX=15.2817 EndY=-59.5497 EndZ=0
    g18: LineSegment StartX=15.2817 StartY=-59.5497 StartZ=0 EndX=14.1518 EndY=-63.1814 EndZ=0
    g19: LineSegment StartX=15.2817 StartY=-56.1814 StartZ=0 EndX=15.2817 EndY=-59.5497 EndZ=0
    g20: LineSegment StartX=21.9059 StartY=-65.0911 StartZ=0 EndX=21.9059 EndY=-67.1814 EndZ=0
    g21: LineSegment StartX=23.0941 StartY=-61.2717 StartZ=0 EndX=26.5 EndY=-61.2717 EndZ=0
    g22: LineSegment StartX=21.9059 StartY=-67.1814 StartZ=0 EndX=21.9059 EndY=-65.0911 EndZ=0
    g23: LineSegment StartX=21.9059 StartY=-65.0911 StartZ=0 EndX=23.0941 EndY=-61.2717 EndZ=0
    g24: LineSegment StartX=23.0941 StartY=-61.2717 StartZ=0 EndX=15.2817 EndY=-59.5497 EndZ=0
    g25: LineSegment StartX=15.2817 StartY=-59.5497 StartZ=0 EndX=14.1518 EndY=-63.1814 EndZ=0
    g26: LineSegment StartX=14.1518 StartY=-63.1814 StartZ=0 EndX=0 EndY=-63.1814 EndZ=0
    g27: LineSegment StartX=0 StartY=-63.1814 StartZ=0 EndX=0 EndY=-67.1814 EndZ=0
    g28: LineSegment StartX=0 StartY=-67.1814 StartZ=0 EndX=21.9059 EndY=-67.1814 EndZ=0
  constraints (77):
    c: Coincident(g0,g1)
    c: Coincident(g1,g2)
    c: Coincident(g2,g3)
    c: Coincident(g3,g0)
    c: Horizontal(g0)
    c: Horizontal(g2)
    c: Vertical(g1)
    c: Vertical(g3)
    c: PointOnObject(g0,g-2)
    c: Distance(g0) = 22.5
    c: Distance(g1) = 4
    c: Coincident(g4,g5)
    c: Coincident(g5,g6)
    c: Coincident(g6,g7)
    c: Coincident(g7,g4)
    c: Horizontal(g4)
    c: Horizontal(g6)
    c: Vertical(g5)
    c: Vertical(g7)
    c: Coincident(g4,g0)
    c: Distance(g7) = 5
    c: Distance(g6) = 4
    c: Coincident(g8,g9)
    c: Coincident(g9,g10)
    c: Coincident(g10,g11)
    c: Coincident(g11,g8)
    c: Horizontal(g8)
    c: Horizontal(g10)
    c: Vertical(g9)
    c: Vertical(g11)
    c: Coincident(g8,g0)
    c: PointOnObject(g9,g-2)
    c: Distance(g9) = 7
    c: Coincident(g12,g9)
    c: Coincident(g12,g0)
    c: Coincident(g13,g0)
    c: Perpendicular(g13,g12)
    c: Distance(g13) = 2
    c: Coincident(g14,g0)
    c: Distance(g14) = 2
    c: Perpendicular(g14,g12)
    c: Coincident(g15,g14)
    c: Coincident(g15,g9)
    c: Coincident(g16,g13)
    c: Coincident(g16,g9)
    c: Coincident(g17,g14)
    c: PointOnObject(g17,g15)
    c: Distance(g17) = 8
    c: Coincident(g18,g17)
    c: PointOnObject(g18,g0)
    c: Perpendicular(g18,g12)
    c: PointOnObject(g19,g10)
    c: Coincident(g19,g17)
    c: Vertical(g19)
    c: Coincident(g20,g13)
    c: PointOnObject(g20,g2)
    c: Vertical(g20)
    c: Coincident(g21,g14)
    c: PointOnObject(g21,g5)
    c: Horizontal(g21)
    c: Angle(g15,g10) = 0.216946
    c: Angle(g12,g10) = 0.301619
    c: Angle(g9,g12) = 1.26918
    c: Coincident(g22,g20)
    c: Coincident(g22,g13)
    c: Coincident(g22,g23)
    c: Coincident(g23,g14)
    c: Coincident(g23,g24)
    c: Coincident(g24,g17)
    c: Coincident(g24,g25)
    c: Coincident(g25,g18)
    c: Coincident(g26,g25)
    c: Coincident(g26,g0)
    c: Coincident(g27,g26)
    c: Coincident(g27,g2)
    c: Coincident(g28,g27)
    c: Coincident(g28,g22)
FEATURE [PartDesign::Revolution] Revolution017
  Angle = 360
  Axis = (0,-9e-16,4)
  Base = (0,1.49e-14,-67.1814)
  Placement = pos=(0,0,0) rot=(1,0,0;1.5708rad)
  Profile = -> Sketch017
  ReferenceAxis = -> Sketch017 [Axis3]
  Reversed = true
FEATURE [PartDesign::Body] Body015
  Group = -> [Revolution017,Sketch017]
  Origin = -> Origin015
  Placement = pos=(0,0,-199.6) rot=(0,0,1;0rad)
  Tip = -> Revolution017
FEATURE [Part::Cylinder] Cylinder707  label="Válec707"
  Angle = 360
  AttacherType = Attacher::AttachEngine3D
  Height = 17
  Placement = pos=(0,83,252) rot=(0,0,1;0rad)
  Radius = 8
FEATURE [Part::Cylinder] Cylinder708  label="Válec708"
  Angle = 360
  AttacherType = Attacher::AttachEngine3D
  Height = 40
  Placement = pos=(0,83,232) rot=(0,0,1;0rad)
  Radius = 2.65
FEATURE [Part::Cut] Cut287
  Base = -> Cylinder707
  Tool = -> Cylinder708
FEATURE [Part::Cylinder] Cylinder709  label="Válec709"
  Angle = 360
  AttacherType = Attacher::AttachEngine3D
  Height = 40
  Placement = pos=(0,83,15) rot=(0,0,1;0rad)
  Radius = 2.65
FEATURE [Part::FeaturePython] wormgear032  # WARN: FeaturePython — macro-defined, semantics opaque (R4)
  AttacherType = Attacher::AttachEngine3D
  Placement = pos=(0,83,32) rot=(0,0,1;0.106465rad)
  beta = 44.3704
  clearance = 0.25
  diameter = 46
  head = 0
  height = 5
  module = 1.5
  pressure_angle = 20
  reverse_pitch = true
  teeth = 30
  version = 0.0.3
FEATURE [Part::Cut] Cut288
  Base = -> wormgear032
  Tool = -> Cylinder709
FEATURE [Part::FeaturePython] wormgear033  # WARN: FeaturePython — macro-defined, semantics opaque (R4)
  AttacherType = Attacher::AttachEngine3D
  Placement = pos=(0,83,37) rot=(0,0,1;0.302815rad)
  beta = 44.3704
  clearance = 0.25
  diameter = 46
  head = 0
  height = 5
  module = 1.5
  pressure_angle = 20
  reverse_pitch = false
  teeth = 30
  version = 0.0.3
FEATURE [Part::FeaturePython] bevelgear014  # WARN: FeaturePython — macro-defined, semantics opaque (R4)
  AttacherType = Attacher::AttachEngine3D
  Placement = pos=(0,0,-254.4) rot=(1,0,0;3.14159rad)
  backlash = 0
  beta = 12
  clearance = 0.1
  height = 16
  module = 0.1
  numpoints = 6
  pitch_angle = 72.71
  pressure_angle = 21
  reset_origin = true
  teeth = 36
  version = 0.0.3
FEATURE [Part::Common] Common005
  Base = -> Body015
  Placement = pos=(0,83,507) rot=(0,0,1;0rad)
  Tool = -> bevelgear014
FEATURE [Part::Cylinder] Cylinder710  label="Válec710"
  Angle = 360
  AttacherType = Attacher::AttachEngine3D
  Height = 40
  Placement = pos=(0,83,15) rot=(0,0,1;0rad)
  Radius = 2.65
FEATURE [Part::Cut] Cut289
  Base = -> wormgear033
  Tool = -> Cylinder710
FEATURE [Part::Compound] Compound381
  Links = -> [Cut288,Cut289]
  Placement = pos=(0,0,200) rot=(0,0,1;0rad)
FEATURE [Part::Cylinder] Cylinder711  label="Válec711"
  Angle = 360
  AttacherType = Attacher::AttachEngine3D
  Height = 10
  Placement = pos=(0,83,242) rot=(0,0,1;0rad)
  Radius = 15.1
FEATURE [Part::Cylinder] Cylinder712  label="Válec712"
  Angle = 360
  AttacherType = Attacher::AttachEngine3D
  Height = 30
  Placement = pos=(0,83,232) rot=(0,0,1;0rad)
  Radius = 2.65
FEATURE [Part::Cut] Cut290
  Base = -> Cylinder711
  Tool = -> Cylinder712
FEATURE [Part::Cylinder] Cylinder713  label="Válec713"
  Angle = 360
  AttacherType = Attacher::AttachEngine3D
  Height = 10
  Placement = pos=(0,83,232) rot=(0,0,1;0rad)
  Radius = 25
FEATURE [Part::Cut] Cut291
  Base = -> Common005
  Tool = -> Cylinder713
FEATURE [Part::Cylinder] Cylinder714  label="Válec714"
  Angle = 360
  AttacherType = Attacher::AttachEngine3D
  Height = 40
  Placement = pos=(0,83,220) rot=(0,0,1;0rad)
  Radius = 2.65
FEATURE [Part::Cut] Cut292
  Base = -> Cut291
  Tool = -> Cylinder714
FEATURE [Part::Compound] Compound382  label="Base_rear-gear-large-solid-1.5"
  Links = -> [Cut290,Cut292,Cut287,Compound381]
FEATURE [Mesh::Feature] Mesh  label="Base_rear-gear-large-solid-1.5 (Meshed)"
